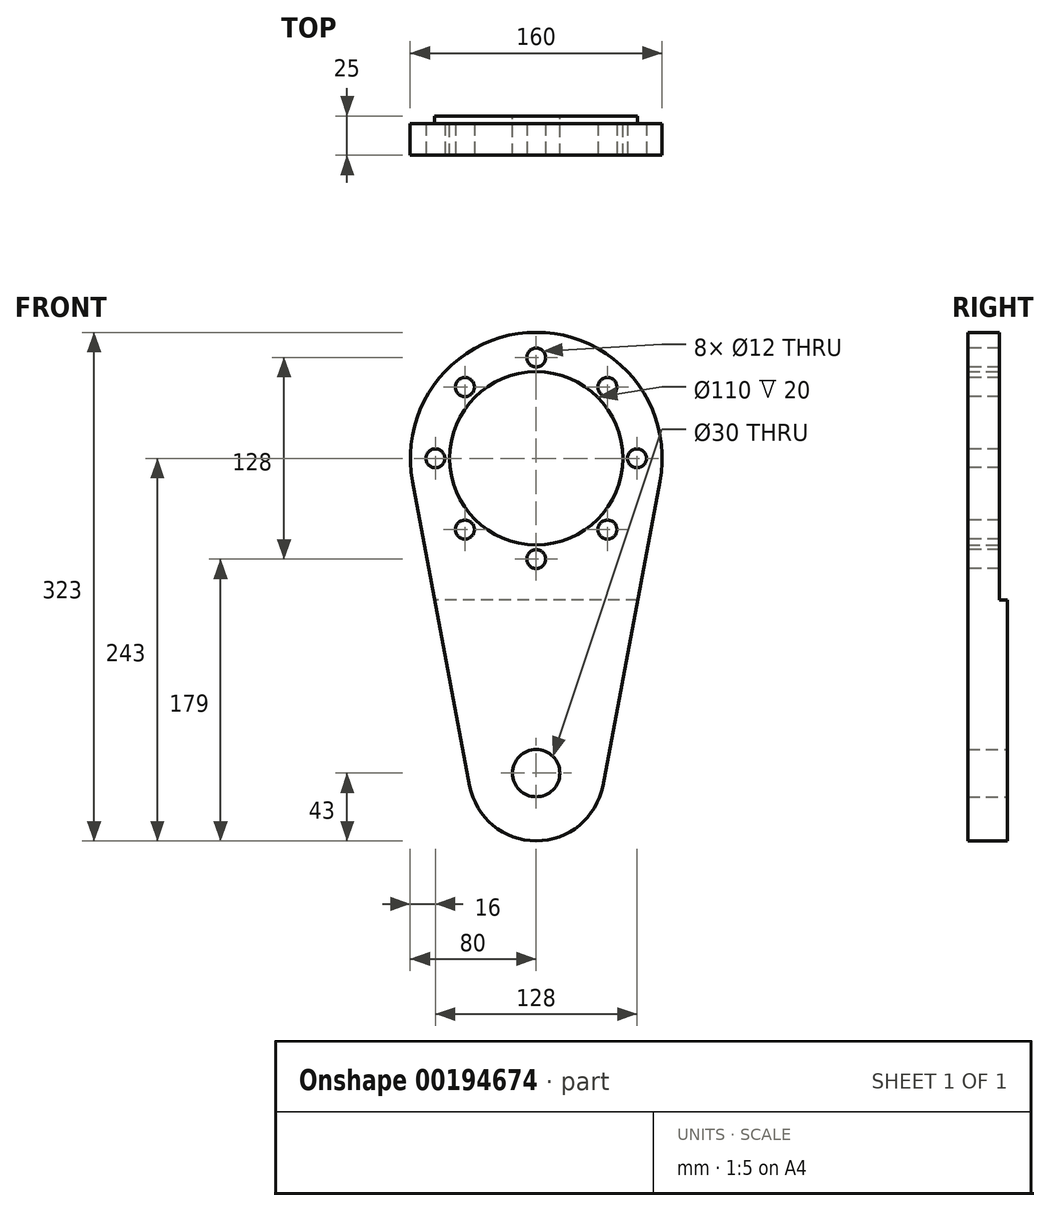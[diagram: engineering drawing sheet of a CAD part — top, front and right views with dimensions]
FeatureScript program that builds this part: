
annotation { "Feature Type Name" : "Feature", "Feature Type Description" : "" }
export const myFeature = defineFeature(function(context is Context, id is Id, definition is map)
    precondition{}
    {
        {
            var Q0;
            Q0=qCreatedBy(makeId("Front.planeOp"),FACE);
            var sketch = newSketch(context, id + "F0", { "sketchPlane" : qUnion([Q0])});
            skCircle(sketch, "E0", {"center": v(0, 0) * mm, "radius": 55 * mm});
            skCircle(sketch, "E1", {"center": v(0, -200) * mm, "radius": 15 * mm});
            skLineSegment(sketch, "E2", {"start": v(-78.62, -14.8) * mm, "end": v(-42.26, -207.96) * mm});
            skLineSegment(sketch, "E3", {"start": v(42.26, -207.96) * mm, "end": v(78.62, -14.8) * mm});
            skArc(sketch, "E4", {"start": v(78.62, -14.8) * mm, "mid": v(0, 80) * mm, "end": v(-78.62, -14.8) * mm});
            skArc(sketch, "E5", {"start": v(-42.26, -207.96) * mm, "mid": v(0, -243) * mm, "end": v(42.26, -207.96) * mm});
            skSolve(sketch);
        }
        {
            var Q0;
            Q0=makeQuery(id+"F0.imprint","IMPRINT",FACE,{"disambiguationData":[TD([[makeQuery(id+"F0.imprint","IMPRINT",EDGE,{"derivedFrom":sQuery(id+"F0.wireOp",EDGE,"E1")}),-1.0]])]});
            var Q1;
            Q1=makeQuery(id+"F0.imprint","IMPRINT",FACE,{"disambiguationData":[TD([[makeQuery(id+"F0.imprint","IMPRINT",EDGE,{"derivedFrom":sQuery(id+"F0.wireOp",EDGE,"E0")}),-1.0]])]});
            extrude(context, id + "F1", {"entities" : qUnion([Q0, Q1]), "depth" : 25 * mm, "offsetDistance" : 25 * mm});
        }
        {
            var Q0;
            Q0=makeQuery(id+"F1.opExtrude","CAP_FACE",FACE,{"disambiguationData":[OSD([sQuery(id+"F0.wireOp",EDGE,"E0"),sQuery(id+"F0.wireOp",EDGE,"E1"),sQuery(id+"F0.wireOp",EDGE,"E2"),sQuery(id+"F0.wireOp",EDGE,"E3"),sQuery(id+"F0.wireOp",EDGE,"E4"),sQuery(id+"F0.wireOp",EDGE,"E5")])],"isStart":true});
            var sketch = newSketch(context, id + "F2", { "sketchPlane" : qUnion([Q0])});
            skLineSegment(sketch, "E6", {"start": v(-64.46, -90) * mm, "end": v(64.46, -90) * mm});
            skSolve(sketch);
        }
        {
            var Q0;
            {var subQ2=sQuery(id+"F2.wireOp",EDGE,"E6");Q0=makeQuery(id+"F2.imprint","IMPRINT",FACE,{"disambiguationData":[TD([[makeQuery(id+"F2.imprint","IMPRINT",EDGE,{"derivedFrom":subQ2}),1.0]])]});}
            extrude(context, id + "F3", {"entities" : qUnion([Q0]), "operationType" : NewBodyOperationType.REMOVE, "oppositeDirection" : true, "depth" : 5 * mm, "offsetDistance" : 25 * mm});
        }
        {
            var Q0;
            Q0=makeQuery(id+"F1.opExtrude","CAP_FACE",FACE,{"disambiguationData":[OSD([sQuery(id+"F0.wireOp",EDGE,"E0"),sQuery(id+"F0.wireOp",EDGE,"E1"),sQuery(id+"F0.wireOp",EDGE,"E2"),sQuery(id+"F0.wireOp",EDGE,"E3"),sQuery(id+"F0.wireOp",EDGE,"E4"),sQuery(id+"F0.wireOp",EDGE,"E5")])],"isStart":false});
            var sketch = newSketch(context, id + "F4", { "sketchPlane" : qUnion([Q0])});
            skCircle(sketch, "E7", {"center": v(0, 64) * mm, "radius": 6 * mm});
            skCircle(sketch, "E8.1.0", {"center": v(-45.25, 45.25) * mm, "radius": 6 * mm});
            skCircle(sketch, "E8.2.0", {"center": v(-64, 0) * mm, "radius": 6 * mm});
            skCircle(sketch, "E8.3.0", {"center": v(-45.25, -45.25) * mm, "radius": 6 * mm});
            skCircle(sketch, "E8.4.0", {"center": v(0, -64) * mm, "radius": 6 * mm});
            skCircle(sketch, "E8.5.0", {"center": v(45.25, -45.25) * mm, "radius": 6 * mm});
            skCircle(sketch, "E8.6.0", {"center": v(64, 0) * mm, "radius": 6 * mm});
            skCircle(sketch, "E8.7.0", {"center": v(45.25, 45.25) * mm, "radius": 6 * mm});
            skPoint(sketch, "E8.center", {"position": v(0, 0) * mm});
            skSolve(sketch);
        }
        {
            var Q0;
            Q0=makeQuery(id+"F4.imprint","IMPRINT",FACE,{"disambiguationData":[TD([[makeQuery(id+"F4.imprint","IMPRINT",EDGE,{"derivedFrom":sQuery(id+"F4.wireOp",EDGE,"E7")}),1.0]])]});
            var Q1;
            Q1=makeQuery(id+"F4.imprint","IMPRINT",FACE,{"disambiguationData":[TD([[makeQuery(id+"F4.imprint","IMPRINT",EDGE,{"derivedFrom":sQuery(id+"F4.wireOp",EDGE,"E8.7.0")}),1.0]])]});
            var Q2;
            Q2=makeQuery(id+"F4.imprint","IMPRINT",FACE,{"disambiguationData":[TD([[makeQuery(id+"F4.imprint","IMPRINT",EDGE,{"derivedFrom":sQuery(id+"F4.wireOp",EDGE,"E8.6.0")}),1.0]])]});
            var Q3;
            Q3=makeQuery(id+"F4.imprint","IMPRINT",FACE,{"disambiguationData":[TD([[makeQuery(id+"F4.imprint","IMPRINT",EDGE,{"derivedFrom":sQuery(id+"F4.wireOp",EDGE,"E8.5.0")}),1.0]])]});
            var Q4;
            Q4=makeQuery(id+"F4.imprint","IMPRINT",FACE,{"disambiguationData":[TD([[makeQuery(id+"F4.imprint","IMPRINT",EDGE,{"derivedFrom":sQuery(id+"F4.wireOp",EDGE,"E8.4.0")}),1.0]])]});
            var Q5;
            Q5=makeQuery(id+"F4.imprint","IMPRINT",FACE,{"disambiguationData":[TD([[makeQuery(id+"F4.imprint","IMPRINT",EDGE,{"derivedFrom":sQuery(id+"F4.wireOp",EDGE,"E8.3.0")}),1.0]])]});
            var Q6;
            Q6=makeQuery(id+"F4.imprint","IMPRINT",FACE,{"disambiguationData":[TD([[makeQuery(id+"F4.imprint","IMPRINT",EDGE,{"derivedFrom":sQuery(id+"F4.wireOp",EDGE,"E8.2.0")}),1.0]])]});
            var Q7;
            Q7=makeQuery(id+"F4.imprint","IMPRINT",FACE,{"disambiguationData":[TD([[makeQuery(id+"F4.imprint","IMPRINT",EDGE,{"derivedFrom":sQuery(id+"F4.wireOp",EDGE,"E8.1.0")}),1.0]])]});
            extrude(context, id + "F5", {"entities" : qUnion([Q0, Q1, Q2, Q3, Q4, Q5, Q6, Q7]), "operationType" : NewBodyOperationType.REMOVE, "oppositeDirection" : true, "depth" : 25 * mm, "offsetDistance" : 25 * mm});
        }
    });
